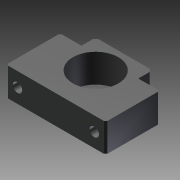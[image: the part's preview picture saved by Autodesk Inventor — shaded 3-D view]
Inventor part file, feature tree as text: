
AUTODESK INVENTOR PART (.ipt)
format: ipt  version: 2016 (Build 200138000, 138)  size: 126,976 bytes
history: native  units: mm
features: other x14, sketch x4, hole x3, extrude x1
ambient origin geometry x8: Origin, YZ Plane, XZ Plane, XY Plane, X Axis, Y Axis, Z Axis, Center Point
bodies: Solid1 (feature_tree)
feature tree (22):
  extrude  "Extrusion1"  TaperAngle=0.0deg  [1 undecoded]
  hole  "Hole1"  [1 undecoded]
  hole  "Hole2"  [1 undecoded]
  hole  "Hole3"  [1 undecoded]
  other  "bf_1_XY"
  other  "bf_1_YZ"
  other  "bf_1_ZX"
  other  "bf_1_X"
  other  "bf_1_Y"
  other  "bf_1_Z"
  other  "bf_1_Center"
  other  "bf_2x_XY"
  other  "bf_2x_YZ"
  other  "bf_2x_ZX"
  other  "bf_2x_X"
  other  "bf_2x_Y"
  other  "bf_2x_Z"
  other  "bf_2x_Center"
  sketch  "Sketch_1"  dims[d0=20.0mm d1=0.0mm]
  sketch  "Sketch2"  dims[d2=6.6mm d3=6.0mm d4=11.0mm d5=6.5mm d6=90.0deg d7=38.0mm d8=0.0mm]
  sketch  "Sketch3"  dims[d9=6.6mm d10=6.0mm d11=11.0mm d12=6.5mm d13=90.0deg d14=38.0mm d15=0.0mm]
  sketch  "Sketch4"  dims[d16=32.0mm d17=6.0mm d18=4.0mm d19=2.0mm d20=90.0deg d21=20.0mm d22=0.0mm d23=0.0mm]
note: 4 required parameter values undecoded (feature->parameter linkage not recoverable at this tier; creation-order binding heuristic only, values carry confidence <= 0.55)
